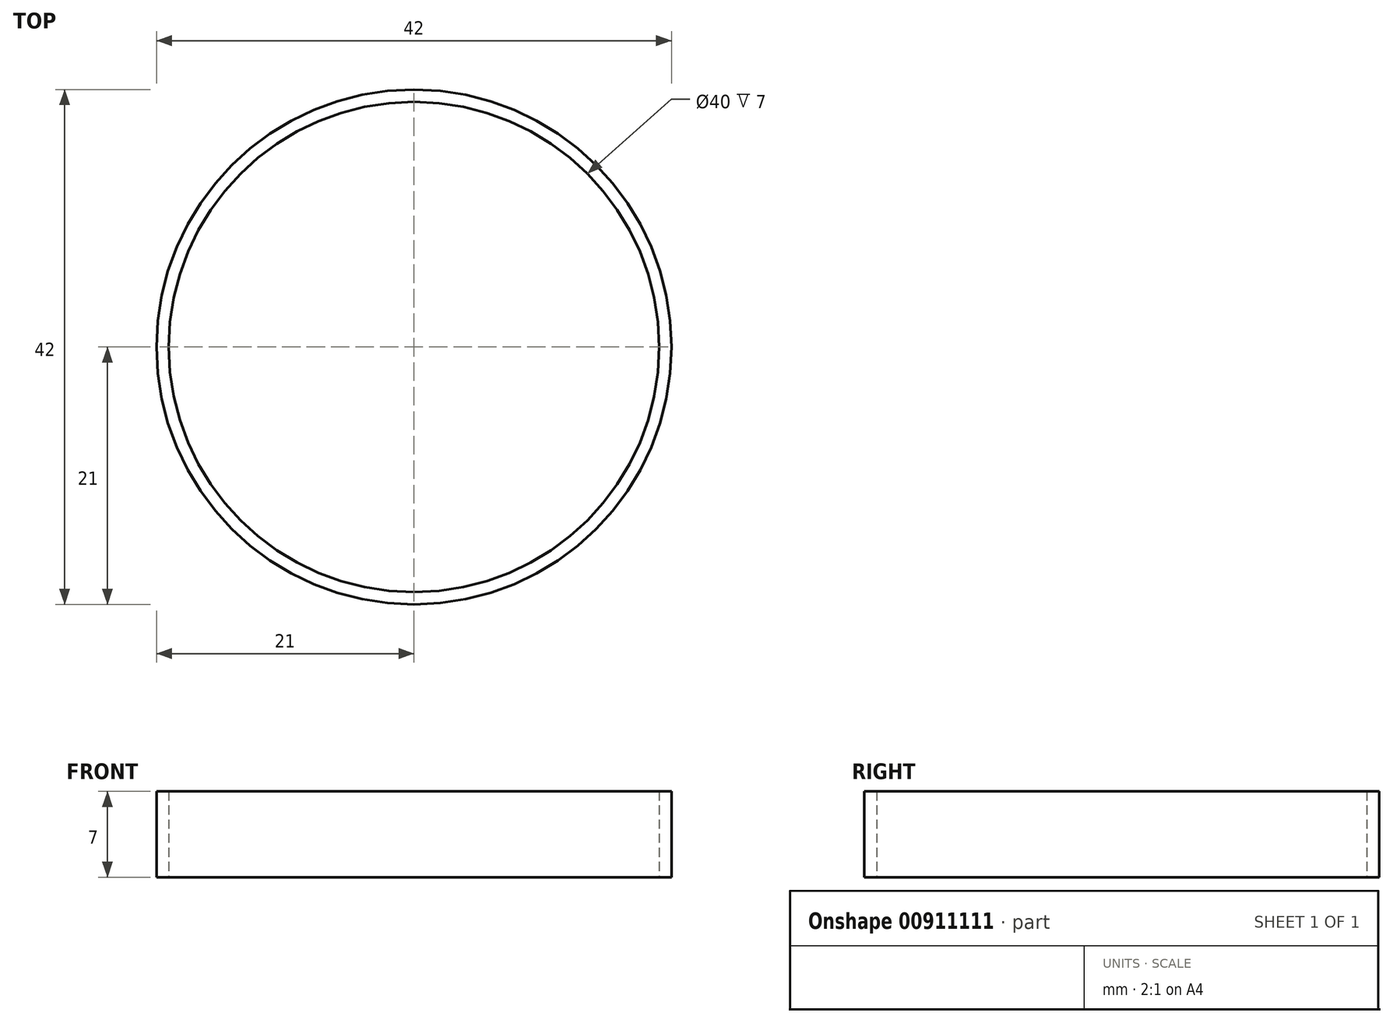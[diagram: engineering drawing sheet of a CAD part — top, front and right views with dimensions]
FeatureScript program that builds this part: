
annotation { "Feature Type Name" : "Feature", "Feature Type Description" : "" }
export const myFeature = defineFeature(function(context is Context, id is Id, definition is map)
    precondition{}
    {
        {
            var Q0;
            Q0=qCreatedBy(makeId("Top.planeOp"),FACE);
            var sketch = newSketch(context, id + "F0", { "sketchPlane" : qUnion([Q0])});
            skCircle(sketch, "E0", {"center": v(0, 0) * mm, "radius": 20 * mm});
            skCircle(sketch, "E1", {"center": v(0, 0) * mm, "radius": 21 * mm});
            skSolve(sketch);
        }
        {
            var Q0;
            Q0 = qSketchRegion(id + "F0", true);
            extrude(context, id + "F1", {"entities" : qUnion([Q0]), "depth" : 7 * mm, "offsetDistance" : 25 * mm});
        }
    });
